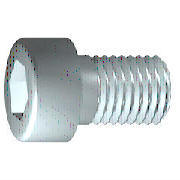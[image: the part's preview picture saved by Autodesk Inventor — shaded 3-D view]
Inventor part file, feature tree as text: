
AUTODESK INVENTOR PART (.ipt)
format: ipt  version: 2015 (Build 190159000, 159)  size: 188,416 bytes
history: native  units: mm (DEFAULTED — no unit token found)
features: sketch x2, extrude x1, plane x1, fillet x1
ambient origin geometry x7: Origin, YZ Plane, XY Plane, X Axis, Y Axis, Z Axis, Center Point
bodies: Solid1 (feature_tree), Body (feature_tree)
feature tree (5):
  extrude  "Slot"  Depth=3.0mm
  plane  "Work Plane1"
  fillet  "Fillet2"  Radius=3.0mm
  sketch  "Sketch1"  dims[d1=18.0mm d2=0.306825mm d3=3.0mm]
  sketch  "Sketch2"  dims[d4=1.3mm d5=60.0deg d6=3.0mm d7=3.0mm d8=2.886751mm d9=5.5mm d10=90.0deg d11=10.0mm d12=0.0mm d13=18.0mm d14=0.0mm d15=0.306725mm d16=0.306725mm d17=0.3mm d19=0.0mm d26=30.0mm d27=45.0deg d28=0.0mm d29=0.0mm d30=0.1mm]
